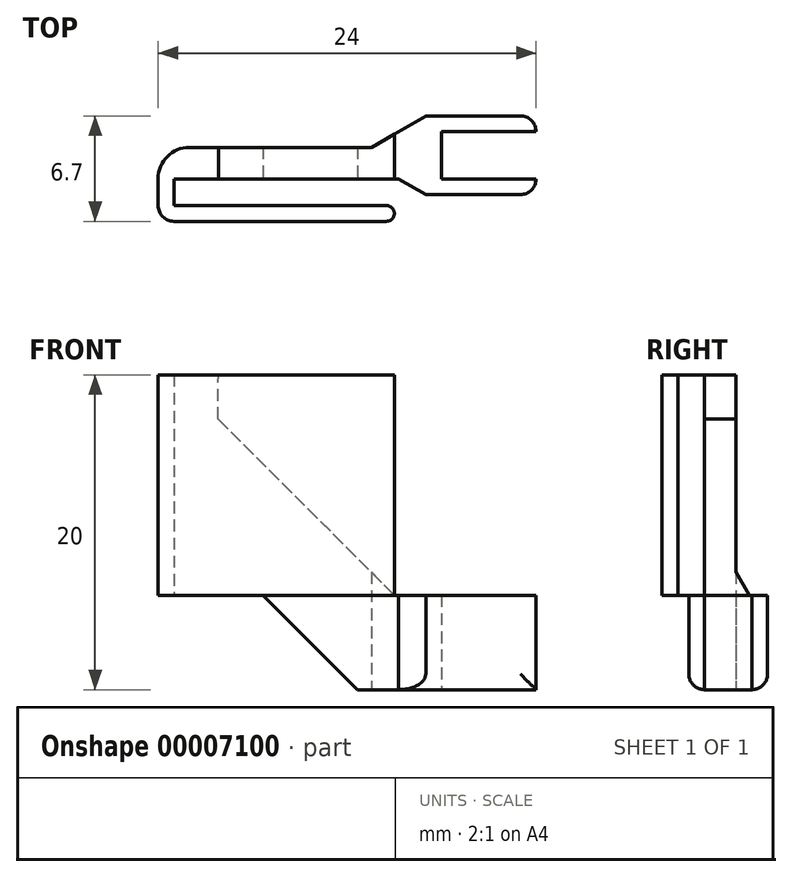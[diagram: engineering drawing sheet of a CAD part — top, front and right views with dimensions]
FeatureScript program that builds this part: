
annotation { "Feature Type Name" : "Feature", "Feature Type Description" : "" }
export const myFeature = defineFeature(function(context is Context, id is Id, definition is map)
    precondition{}
    {
        {
            var Q0;
            Q0=qCreatedBy(makeId("Top.planeOp"),FACE);
            var sketch = newSketch(context, id + "F0", { "sketchPlane" : qUnion([Q0])});
            skLineSegment(sketch, "E0", {"start": v(15.7, 0) * mm, "end": v(9.7, 0) * mm});
            skLineSegment(sketch, "E1", {"start": v(9.7, 0) * mm, "end": v(9.7, 3) * mm});
            skLineSegment(sketch, "E2", {"start": v(9.7, 3) * mm, "end": v(15.7, 3) * mm});
            skLineSegment(sketch, "E3", {"start": v(15.7, 3) * mm, "end": v(15.7, 4) * mm});
            skLineSegment(sketch, "E4", {"start": v(15.7, 4) * mm, "end": v(8.7, 4) * mm});
            skLineSegment(sketch, "E5", {"start": v(8.7, 4) * mm, "end": v(5.23, 2) * mm});
            skLineSegment(sketch, "E6", {"start": v(5.23, 2) * mm, "end": v(-6.3, 2) * mm});
            skLineSegment(sketch, "E7", {"start": v(-8.3, 0) * mm, "end": v(-8.3, -1.7) * mm});
            skLineSegment(sketch, "E8", {"start": v(-7.3, -2.7) * mm, "end": v(6.2, -2.7) * mm});
            skLineSegment(sketch, "E9", {"start": v(6.7, -2.2) * mm, "end": v(6.7, -2.2) * mm});
            skLineSegment(sketch, "E10", {"start": v(6.2, -1.7) * mm, "end": v(-7.3, -1.7) * mm});
            skLineSegment(sketch, "E11", {"start": v(-7.3, -1.7) * mm, "end": v(-7.3, 0) * mm});
            skLineSegment(sketch, "E12", {"start": v(-7.3, 0) * mm, "end": v(6.96, 0) * mm});
            skLineSegment(sketch, "E13", {"start": v(6.96, 0) * mm, "end": v(8.7, -1) * mm});
            skLineSegment(sketch, "E14", {"start": v(8.7, -1) * mm, "end": v(15.7, -1) * mm});
            skLineSegment(sketch, "E15", {"start": v(15.7, -1) * mm, "end": v(15.7, 0) * mm});
            skPoint(sketch, "E16.visualSharp", {"position": v(-8.3, 2) * mm});
            skArc(sketch, "E16.filletArc", {"start": v(-6.3, 2) * mm, "mid": v(-7.72, 1.41) * mm, "end": v(-8.3, 0) * mm});
            skPoint(sketch, "E17.visualSharp", {"position": v(-8.3, -2.7) * mm});
            skArc(sketch, "E17.filletArc", {"start": v(-8.3, -1.7) * mm, "mid": v(-8.01, -2.4) * mm, "end": v(-7.3, -2.7) * mm});
            skPoint(sketch, "E18.visualSharp", {"position": v(6.7, -2.7) * mm});
            skArc(sketch, "E18.filletArc", {"start": v(6.2, -2.7) * mm, "mid": v(6.55, -2.55) * mm, "end": v(6.7, -2.2) * mm});
            skPoint(sketch, "E19.visualSharp", {"position": v(6.7, -1.7) * mm});
            skArc(sketch, "E19.filletArc", {"start": v(6.7, -2.2) * mm, "mid": v(6.55, -1.85) * mm, "end": v(6.2, -1.7) * mm});
            skSolve(sketch);
        }
        {
            var Q0;
            Q0 = qSketchRegion(id + "F0", true);
            extrude(context, id + "F1", {"entities" : qUnion([Q0]), "depth" : 20 * mm});
        }
        {
            var Q0;
            Q0=makeQuery(id+"F1.opExtrude","SWEPT_FACE",FACE,{"disambiguationData":[OSD([sQuery(id+"F0.wireOp",EDGE,"E14")])]});
            var sketch = newSketch(context, id + "F2", { "sketchPlane" : qUnion([Q0])});
            skLineSegment(sketch, "E20", {"start": v(-4.5, 17.2) * mm, "end": v(6.7, 6) * mm});
            skLineSegment(sketch, "E21", {"start": v(6.7, 6) * mm, "end": v(18.7, 6) * mm});
            skLineSegment(sketch, "E22", {"start": v(18.7, 6) * mm, "end": v(18.7, 26) * mm});
            skLineSegment(sketch, "E23", {"start": v(18.7, 26) * mm, "end": v(-4.43, 26) * mm});
            skLineSegment(sketch, "E24", {"start": v(-4.43, 26) * mm, "end": v(-4.5, 17.2) * mm});
            skLineSegment(sketch, "E25", {"start": v(-21.87, -6.23) * mm, "end": v(8.27, -6.23) * mm});
            skSolve(sketch);
        }
        {
            var Q0;
            Q0 = qSketchRegion(id + "F2", true);
            extrude(context, id + "F3", {"entities" : qUnion([Q0]), "operationType" : NewBodyOperationType.REMOVE, "endBound" : BoundingType.THROUGH_ALL, "oppositeDirection" : true, "depth" : 25 * mm});
        }
        {
            var Q0;
            Q0=makeQuery(id+"F1.opExtrude","SWEPT_EDGE",EDGE,{"disambiguationData":[OSD([sQuery(id+"F0.wireOp",EDGE,"E14"),sQuery(id+"F0.wireOp",EDGE,"E15")])]});
            var Q1;
            Q1=makeQuery(id+"F1.opExtrude","SWEPT_EDGE",EDGE,{"disambiguationData":[OSD([sQuery(id+"F0.wireOp",EDGE,"E3"),sQuery(id+"F0.wireOp",EDGE,"E4")])]});
            var Q2;
            Q2=makeQuery(id+"F1.opExtrude","CAP_EDGE",EDGE,{"disambiguationData":[OSD([sQuery(id+"F0.wireOp",EDGE,"E14")])],"isStart":true});
            var Q3;
            Q3=makeQuery(id+"F1.opExtrude","CAP_EDGE",EDGE,{"disambiguationData":[OSD([sQuery(id+"F0.wireOp",EDGE,"E4")])],"isStart":true});
            fillet(context, id + "F4", {"entities" : qUnion([Q0, Q1, Q2, Q3]), "radius" : 1 * mm, "tangentPropagation" : true, "allowEdgeOverflow" : false});
        }
        {
            var Q0;
            Q0=makeQuery(id+"F1.opExtrude","SWEPT_FACE",FACE,{"disambiguationData":[OSD([sQuery(id+"F0.wireOp",EDGE,"E8")])]});
            var sketch = newSketch(context, id + "F5", { "sketchPlane" : qUnion([Q0])});
            skLineSegment(sketch, "E26", {"start": v(-20.76, 6) * mm, "end": v(-1.64, 6) * mm});
            skLineSegment(sketch, "E27", {"start": v(-1.64, 6) * mm, "end": v(4.36, 0) * mm});
            skLineSegment(sketch, "E28", {"start": v(4.36, 0) * mm, "end": v(4.36, -4.18) * mm});
            skLineSegment(sketch, "E29", {"start": v(4.36, -4.18) * mm, "end": v(-20.88, -4.18) * mm});
            skLineSegment(sketch, "E30", {"start": v(-20.88, -4.18) * mm, "end": v(-20.76, 6) * mm});
            skLineSegment(sketch, "E31.0", {"start": v(6.7, 6) * mm, "end": v(-0.84, 13.54) * mm, "construction": true});
            skLineSegment(sketch, "E32.1", {"start": v(14.7, 6) * mm, "end": v(8.7, 6) * mm, "construction": true});
            skSolve(sketch);
        }
        {
            var Q0;
            Q0 = qSketchRegion(id + "F5", true);
            extrude(context, id + "F6", {"entities" : qUnion([Q0]), "operationType" : NewBodyOperationType.REMOVE, "endBound" : BoundingType.SYMMETRIC, "oppositeDirection" : true, "depth" : 25 * mm});
        }
        {
            var Q0;
            Q0=makeQuery(id+"F1.opExtrude","SWEPT_FACE",FACE,{"disambiguationData":[OSD([sQuery(id+"F0.wireOp",EDGE,"E8")])]});
            var sketch = newSketch(context, id + "F7", { "sketchPlane" : qUnion([Q0])});
            skLineSegment(sketch, "E33", {"start": v(-7.6, 6) * mm, "end": v(6.92, 6) * mm});
            skLineSegment(sketch, "E34", {"start": v(6.92, 6) * mm, "end": v(6.92, 0) * mm});
            skLineSegment(sketch, "E35", {"start": v(6.92, 0) * mm, "end": v(-7.6, 0) * mm});
            skLineSegment(sketch, "E36", {"start": v(-7.6, 0) * mm, "end": v(-7.6, 6) * mm});
            skSolve(sketch);
        }
        {
            var Q0;
            Q0 = qSketchRegion(id + "F7", true);
            var Q1;
            Q1=makeQuery(id+"F1.opExtrude","SWEPT_FACE",FACE,{"disambiguationData":[OSD([sQuery(id+"F0.wireOp",EDGE,"E12")])]});
            extrude(context, id + "F8", {"entities" : qUnion([Q0]), "operationType" : NewBodyOperationType.REMOVE, "endBound" : BoundingType.UP_TO_SURFACE, "oppositeDirection" : true, "endBoundEntityFace" : qUnion([Q1]), "depth" : 25 * mm});
        }
    });
